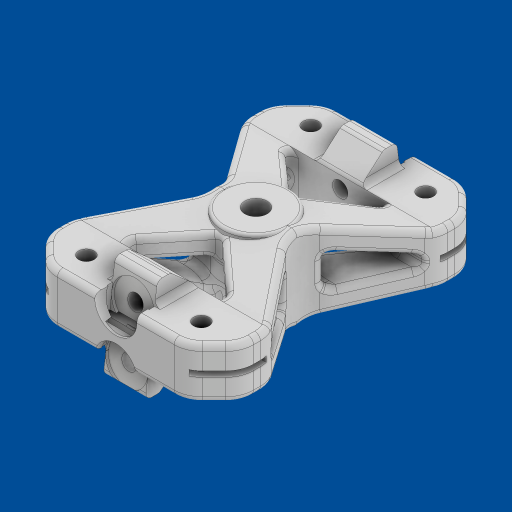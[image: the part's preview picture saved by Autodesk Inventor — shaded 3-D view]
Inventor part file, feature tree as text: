
AUTODESK INVENTOR PART (.ipt)
format: ipt  version: 2023 (Build 270158000, 158)  size: 1,775,104 bytes
history: native  units: mm
features: extrude x18, fillet x16, sketch x6, chamfer x6, plane x1, loft x1, mirror x1, other x1
ambient origin geometry x8: Origin, YZ Plane, XZ Plane, XY Plane, X Axis, Y Axis, Z Axis, Center Point
bodies: Body1 (feature_tree)
feature tree (50):
  sketch  "Sketch1"  dims[d13=261.822mm d14=7.45mm]
  plane  "Work Plane1"
  sketch  "Sketch2"  dims[d15=27.223mm d17=1.0mm]
  extrude  "Extrusion26"  Depth=7.45mm
  extrude  "Extrusion27"  Depth=1.0mm
  extrude  "Extrusion28"  Depth=100.0mm
  loft  "Loft4"
  extrude  "Extrusion30"  Depth=1.0mm
  extrude  "Extrusion31"  Depth=2.0mm
  extrude  "Extrusion32"  Depth=2.0mm
  extrude  "Extrusion33"  Depth=2.0mm
  sketch  "Sketch13"  dims[d23=2.0mm d25=1.0mm]
  extrude  "Extrusion34"  Depth=2.0mm
  extrude  "Extrusion35"  Depth=2.0mm
  extrude  "Extrusion36"  Depth=10.0mm TaperAngle=0.0deg
  extrude  "Extrusion37"  Depth=2.0mm
  fillet  "Fillet8"  Radius=24.0mm
  extrude  "Extrusion38"  Depth=2.0mm TaperAngle=0.0deg
  chamfer  "Chamfer7"  Distance=8.0mm
  chamfer  "Chamfer8"  Distance=19.96mm
  fillet  "Fillet9"  Radius=15.0mm
  mirror  "Mirror1"
  extrude  "Extrusion39"  TaperAngle=0.0deg  [1 undecoded]
  extrude  "Extrusion40"  TaperAngle=0.0deg  [1 undecoded]
  fillet  "Fillet10"  Radius=2.0mm
  fillet  "Fillet11"  Radius=2.0mm
  extrude  "Extrusion41"  Depth=2.0mm TaperAngle=0.0deg
  sketch  "Sketch15"  dims[d28=90.0deg d29=5.5mm d30=15.0mm d31=65.0mm d56=12.0mm d74=1.0mm d75=8.0mm d148=244.423mm d149=41.005864mm d150=244.423mm d151=5.5mm d152=5.5mm d153=5.5mm d154=15.0mm d155=15.0mm d156=18.0mm d157=5.5mm d158=160.0mm d159=10.0mm d160=0.0mm d161=8.0mm d162=24.0mm d163=30.0mm d164=0.0mm d165=8.0mm d166=0.0mm d167=19.96mm d168=15.0mm d169=0.0mm d170=0.0mm d171=90.0deg d172=0.0mm d173=90.0deg d178=2.0mm d179=0.0mm d180=2.0mm d181=15.0mm d182=0.0mm d183=15.0mm d184=0.0mm d185=15.0mm d186=0.0mm d187=15.0mm d188=15.0mm d189=15.0mm d190=2.5mm d191=15.0mm d192=15.0mm d193=5.5mm d194=5.5mm d195=1.0mm d196=0.0mm d197=16.0mm d198=0.0mm d199=15.0mm d200=0.0mm d201=15.0mm d202=0.0mm d203=2.0mm d204=1.0mm d205=0.0mm d206=10.0mm d207=10.0mm d208=45.0deg d209=10.0mm d210=10.0mm d211=45.0deg d212=10.0mm d213=15.0mm d214=0.0mm d215=15.0mm d216=15.0mm d217=0.0mm d218=10.0mm d219=10.0mm d220=30.0mm d221=0.0mm d226=8.0mm d227=7.0mm d228=45.0deg d229=7.0mm d230=8.0mm d231=45.0deg d232=12.0mm d233=9.0mm d234=45.0deg d235=9.0mm d236=12.0mm d237=45.0deg d238=2.0mm d239=2.0mm d240=2.0mm d241=1.0mm d242=2.0mm d244=7.5mm d245=7.5mm d246=90.0deg d247=16.0mm d248=70.0mm d249=0.0mm d256=15.0mm d257=30.0mm d258=0.0mm d259=20.0mm d260=0.0mm d261=20.0mm d262=5.0mm d263=2.0mm d264=2.0mm d266=2.0mm d267=2.0mm d268=2.0mm d76=0.5mm d77=0.872665mm d144=0.5mm d145=0.872665mm d146=0.5mm d147=0.872665mm d243=0.0mm d269=0.0mm d270=0.0mm d271=0.0mm]
  chamfer  "Chamfer9"  Distance=15.0mm
  chamfer  "Chamfer10"  Distance=15.0mm
  chamfer  "Chamfer11"  Distance=15.0mm
  chamfer  "Chamfer12"  Distance=15.0mm
  fillet  "Fillet12"  Radius=15.0mm
  fillet  "Fillet13"  Radius=2.5mm
  fillet  "Fillet14"  Radius=15.0mm
  fillet  "Fillet15"  Radius=15.0mm
  fillet  "Fillet16"  Radius=5.5mm
  extrude  "Extrusion43"  Depth=2.0mm
  extrude  "Extrusion45"  Depth=2.0mm TaperAngle=0.0deg
  extrude  "Extrusion46"  Depth=2.0mm TaperAngle=0.0deg
  fillet  "Fillet17"  Radius=15.0mm
  fillet  "Fillet18"  Radius=15.0mm
  fillet  "Fillet19"  Radius=2.0mm
  fillet  "Fillet20"  Radius=1.0mm
  fillet  "Fillet22"  Radius=10.0mm
  fillet  "Fillet23"  Radius=10.0mm
  fillet  "Fillet24"  Radius=10.0mm
  sketch  "Sketch12"  dims[d21=35.0mm d22=100.0mm]
  other  "Edges5"
  sketch  "Sketch14"  dims[d26=90.0deg d27=1.0mm]
note: 2 required parameter values undecoded (feature->parameter linkage not recoverable at this tier; creation-order binding heuristic only, values carry confidence <= 0.55)
